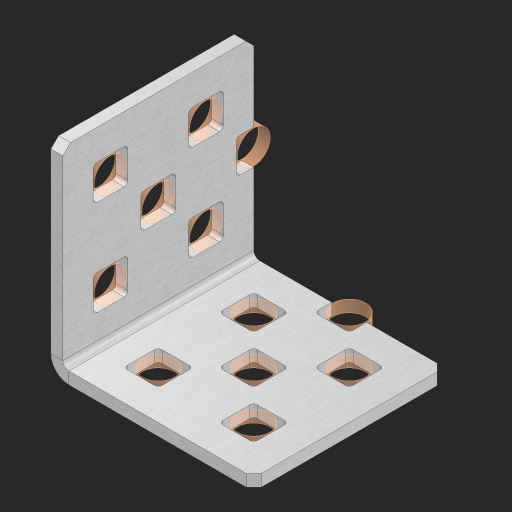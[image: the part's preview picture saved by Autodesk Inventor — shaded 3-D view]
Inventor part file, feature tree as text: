
AUTODESK INVENTOR PART (.ipt)
format: ipt  version: 2023 (Build 270158000, 158)  size: 553,984 bytes
history: native  units: in
note: dims shown in document units (in); Inventor stores cm internally (conversion verified against a paired STEP export)
features: other x18, extrude x10, sheet_metal_op x8, sketch x7, pattern_linear x2, mirror x1, chamfer x1
ambient origin geometry x8: Origin, YZ Plane, XZ Plane, XY Plane, X Axis, Y Axis, Z Axis, Center Point
bodies: Solid1 (feature_tree), Body (feature_tree)
feature tree (47):
  sheet_metal_op  "Flanges"
  sheet_metal_op  "Body Pattern"
  pattern_linear  "Center Pattern"  Spacing1=1.0in  [1 undecoded]
  other  "Arc Length"
  pattern_linear  "Notch Pattern"  Spacing1=0.25in  [1 undecoded]
  other  "Diagonal Plane"
  mirror  "Everything Mirrored"
  chamfer  "End Chamfer"
  sketch  "Sketch1"  dims[d0=1.0in]
  other  "Plate1"
  sketch  "Sketch2"  dims[d1=1.0in]
  other  "Plate2"
  sheet_metal_op  "Bend1"
  sheet_metal_op  "Corner1"
  sketch  "Sketch8"  dims[d2=0.0625in]
  sketch  "Sketch9"  dims[d3=0.0625in]
  other  "Srf91"
  sheet_metal_op  "Body Pattern Sketch"
  other  "Srf92"
  sketch  "Sketch13"  dims[d4=0.0312in]
  sketch  "Sketch15"  dims[d5=0.125in]
  sketch  "Sketch16"  dims[d6=0.0625in d7=1.0in d8=90.0deg d9=0.0312in d10=0.25in d11=0.0625in d12=0.0625in d49=0.182in d50=0.02in d52=0.25in d53=0.0625in d54=0.0in d55=0.172in d56=1.0in d57=0.0in d60=0.7874in d62=0.5in d63=0.7874in d65=0.5in d85=0.1473in d86=0.1782in d89=0.0625in d90=0.0in d91=0.04in d92=0.0491in d95=2.5in d96=0.04in d97=0.25in d98=45.0deg d99=0.25in d106=0.182in d107=0.02in d108=0.5in d110=0.0625in d111=0.0in d112=0.172in d113=0.5in d114=0.0in d117=0.5in d123=0.25in d125=0.25in d126=0.0491in d127=0.1473in d128=0.08in d129=0.04in d130=2.5in]
  other  "Srf786"
  other  "Srf856"
  other  "Srf857"
  other  "Srf889"
  other  "Srf1275"
  other  "Srf1276"
  other  "Srf1278"
  other  "Srf1279"
  other  "Srf1277"
  other  "Srf1285"
  sheet_metal_op  "Body Stamp"
  sheet_metal_op  "Body Circle"
  other  "Center Stamp"
  other  "Center Circle"
  sheet_metal_op  "Notch"
  extrude  "ExtrusionSrf92"  Depth=0.0625in
  extrude  "ExtrusionSrf856"  Depth=0.0625in
  extrude  "ExtrusionSrf857"  Depth=0.182in
  extrude  "ExtrusionSrf889"  Depth=0.02in
  extrude  "ExtrusionSrf1275"  Depth=0.25in
  extrude  "ExtrusionSrf1276"  Depth=0.0625in
  extrude  "ExtrusionSrf1277"  TaperAngle=0.0deg  [1 undecoded]
  extrude  "ExtrusionSrf1278"  Depth=0.25in
  extrude  "ExtrusionSrf1345"  Depth=1.0in TaperAngle=0.0deg
  extrude  "ExtrusionSrf1346"  Depth=0.25in
note: 3 required parameter values undecoded (feature->parameter linkage not recoverable at this tier; creation-order binding heuristic only, values carry confidence <= 0.55)
